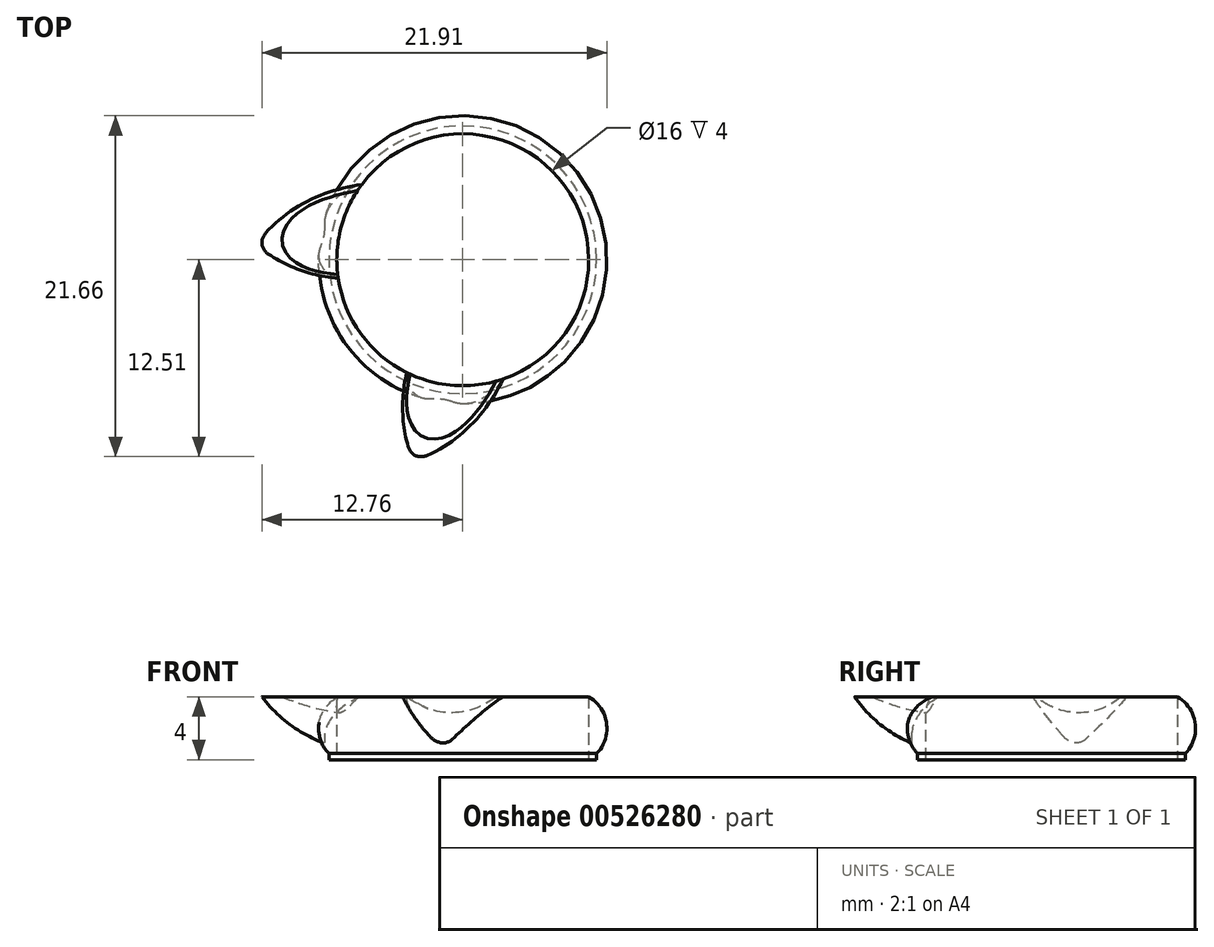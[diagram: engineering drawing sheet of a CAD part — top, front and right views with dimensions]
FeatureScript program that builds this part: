
annotation { "Feature Type Name" : "Feature", "Feature Type Description" : "" }
export const myFeature = defineFeature(function(context is Context, id is Id, definition is map)
    precondition{}
    {
        {
            var Q0;
            Q0=qCreatedBy(makeId("Front.planeOp"),FACE);
            var sketch = newSketch(context, id + "F0", { "sketchPlane" : qUnion([Q0])});
            skArc(sketch, "E0", {"start": v(-8, 2) * mm, "mid": v(-9.15, 0) * mm, "end": v(-8, -2) * mm});
            skLineSegment(sketch, "E1", {"start": v(-8, 2) * mm, "end": v(-8, -2) * mm});
            skLineSegment(sketch, "E2", {"start": v(0, 0) * mm, "end": v(0, 2) * mm, "construction": true});
            skPoint(sketch, "E3", {"position": v(-8, 0) * mm});
            skLineSegment(sketch, "E4", {"start": v(-9.15, 0) * mm, "end": v(-6.85, 0) * mm});
            skLineSegment(sketch, "E5.bottom", {"start": v(-8, -2) * mm, "end": v(-8.5, -2) * mm});
            skLineSegment(sketch, "E5.top", {"start": v(-8, -1.6) * mm, "end": v(-8.5, -1.6) * mm});
            skLineSegment(sketch, "E5.left", {"start": v(-8, -2) * mm, "end": v(-8, -1.6) * mm});
            skLineSegment(sketch, "E5.right", {"start": v(-8.5, -2) * mm, "end": v(-8.5, -1.6) * mm});
            skSolve(sketch);
        }
        {
            var Q0;
            {var subQ0=sQuery(id+"F0.wireOp",EDGE,"E1");var subQ1=sQuery(id+"F0.wireOp",EDGE,"E0");var subQ2=makeQuery(id+"F0.imprint","INTERSECT",VERTEX,{"derivedFrom":[subQ1,subQ0]});Q0=makeQuery(id+"F0.imprint","IMPRINT",FACE,{"disambiguationData":[TD([[makeQuery(id+"F0.imprint","IMPRINT",EDGE,{"disambiguationData":[TD([[subQ2,-1.0]])],"derivedFrom":subQ1}),1.0]])]});}
            var Q1;
            {var subQ3=sQuery(id+"F0.wireOp",EDGE,"E5.top");Q1=makeQuery(id+"F0.imprint","IMPRINT",FACE,{"disambiguationData":[TD([[makeQuery(id+"F0.imprint","IMPRINT",EDGE,{"derivedFrom":subQ3}),-1.0]])]});}
            var Q2;
            {var subQ2=sQuery(id+"F0.wireOp",EDGE,"E5.top");Q2=makeQuery(id+"F0.imprint","IMPRINT",FACE,{"disambiguationData":[TD([[makeQuery(id+"F0.imprint","IMPRINT",EDGE,{"derivedFrom":subQ2}),1.0]])]});}
            var Q3;
            {var subQ0=sQuery(id+"F0.wireOp",EDGE,"E5.bottom");Q3=makeQuery(id+"F0.imprint","IMPRINT",FACE,{"disambiguationData":[TD([[makeQuery(id+"F0.imprint","IMPRINT",EDGE,{"derivedFrom":subQ0}),-1.0]])]});}
            var Q4;
            Q4=sQuery(id+"F0.wireOp",EDGE,"E2");
            revolve(context, id + "F1", {"entities" : qUnion([Q0, Q1, Q2, Q3]), "axis" : qUnion([Q4]), "revolveType" : RevolveType.FULL});
        }
        {
            var Q0;
            Q0=qCreatedBy(makeId("Front.planeOp"),FACE);
            cPlane(context, id + "F2", {"entities" : qUnion([Q0]), "cplaneType" : CPlaneType.OFFSET, "offset" : 6 * mm, "width" : 150 * mm, "height" : 150 * mm});
        }
        {
            var Q0;
            Q0=qCreatedBy(id+"F2.planeOp",FACE);
            var sketch = newSketch(context, id + "F3", { "sketchPlane" : qUnion([Q0])});
            skLineSegment(sketch, "E6", {"start": v(0, 19.97) * mm, "end": v(0, -12.14) * mm});
            skSolve(sketch);
        }
        {
            var Q0;
            Q0=sQuery(id+"F3.wireOp",EDGE,"E6");
            var Q1;
            Q1=qCreatedBy(id+"F2.planeOp",FACE);
            cPlane(context, id + "F4", {"entities" : qUnion([Q0, Q1]), "cplaneType" : CPlaneType.LINE_ANGLE, "offset" : 25 * mm, "angle" : 25 * degree, "width" : 150 * mm, "height" : 150 * mm});
        }
        {
            var Q0;
            Q0=qCreatedBy(id+"F4.planeOp",FACE);
            var sketch = newSketch(context, id + "F5", { "sketchPlane" : qUnion([Q0])});
            skLineSegment(sketch, "E7", {"start": v(-10.54, 7.45) * mm, "end": v(5.46, 7.45) * mm});
            skPoint(sketch, "E8", {"position": v(-2.54, 7.45) * mm});
            skLineSegment(sketch, "E9", {"start": v(-5.54, 2) * mm, "end": v(0.46, 2) * mm});
            skPoint(sketch, "E10", {"position": v(-2.54, 2) * mm});
            skArc(sketch, "E11", {"start": v(-3.2, -1.25) * mm, "mid": v(-2.54, -1.5) * mm, "end": v(-1.88, -1.25) * mm});
            skArc(sketch, "E12", {"start": v(-5.54, 2) * mm, "mid": v(-4.55, 0.24) * mm, "end": v(-3.2, -1.25) * mm});
            skArc(sketch, "E13", {"start": v(-1.88, -1.25) * mm, "mid": v(-0.52, 0.24) * mm, "end": v(0.46, 2) * mm});
            skPoint(sketch, "E14", {"position": v(-2.54, -1.5) * mm});
            skSolve(sketch);
        }
        {
            var Q0;
            Q0=makeQuery(id+"F5.imprint","IMPRINT",FACE,{"disambiguationData":[TD([[makeQuery(id+"F5.imprint","IMPRINT",EDGE,{"derivedFrom":sQuery(id+"F5.wireOp",EDGE,"E9")}),-1.0]])]});
            var Q1;
            Q1=sQuery(id+"F5.wireOp",EDGE,"E7");
            revolve(context, id + "F6", {"operationType" : NewBodyOperationType.ADD, "entities" : qUnion([Q0]), "axis" : qUnion([Q1]), "revolveType" : RevolveType.FULL});
        }
        {
            var Q0;
            Q0=qCreatedBy(makeId("Top.planeOp"),FACE);
            var sketch = newSketch(context, id + "F7", { "sketchPlane" : qUnion([Q0])});
            skCircle(sketch, "E15.0", {"center": v(0, 0) * mm, "radius": 8 * mm});
            skSolve(sketch);
        }
        {
            var Q0;
            Q0=makeQuery(id+"F7.imprint","IMPRINT",FACE,{"disambiguationData":[TD([[makeQuery(id+"F7.imprint","IMPRINT",EDGE,{"derivedFrom":sQuery(id+"F7.wireOp",EDGE,"E15.0")}),1.0]])]});
            extrude(context, id + "F8", {"entities" : qUnion([Q0]), "operationType" : NewBodyOperationType.REMOVE, "endBound" : BoundingType.THROUGH_ALL, "depth" : 25 * mm, "offsetDistance" : 25 * mm, "hasSecondDirection" : true, "secondDirectionBound" : SecondDirectionBoundingType.THROUGH_ALL, "secondDirectionOppositeDirection" : true, "secondDirectionDepth" : 25 * mm});
        }
        {
            var Q0;
            Q0=qCreatedBy(makeId("Top.planeOp"),FACE);
            cPlane(context, id + "F9", {"entities" : qUnion([Q0]), "cplaneType" : CPlaneType.OFFSET, "offset" : 2 * mm, "width" : 150 * mm, "height" : 150 * mm});
        }
        {
            var Q0;
            Q0=qCreatedBy(id+"F9.planeOp",FACE);
            var sketch = newSketch(context, id + "F10", { "sketchPlane" : qUnion([Q0])});
            skLineSegment(sketch, "E16.bottom", {"start": v(-9.55, 0) * mm, "end": v(4.28, 0) * mm});
            skLineSegment(sketch, "E16.top", {"start": v(-9.55, -18.3) * mm, "end": v(4.28, -18.3) * mm});
            skLineSegment(sketch, "E16.left", {"start": v(-9.55, 0) * mm, "end": v(-9.55, -18.3) * mm});
            skLineSegment(sketch, "E16.right", {"start": v(4.28, 0) * mm, "end": v(4.28, -18.3) * mm});
            skSolve(sketch);
        }
        {
            var Q0;
            Q0=makeQuery(id+"F10.imprint","IMPRINT",FACE,{"disambiguationData":[TD([[makeQuery(id+"F10.imprint","IMPRINT",EDGE,{"derivedFrom":sQuery(id+"F10.wireOp",EDGE,"E16.bottom")}),-1.0]])]});
            extrude(context, id + "F11", {"entities" : qUnion([Q0]), "operationType" : NewBodyOperationType.REMOVE, "endBound" : BoundingType.THROUGH_ALL, "depth" : 25 * mm, "offsetDistance" : 25 * mm});
        }
        {
            var Q0;
            Q0=qCreatedBy(makeId("Front.planeOp"),FACE);
            var sketch = newSketch(context, id + "F12", { "sketchPlane" : qUnion([Q0])});
            skLineSegment(sketch, "E17.0", {"start": v(0, 19.97) * mm, "end": v(0, -12.14) * mm});
            skSolve(sketch);
        }
        {
            var Q0;
            Q0=sQuery(id+"F12.wireOp",EDGE,"E17.0");
            var Q1;
            Q1=qCreatedBy(makeId("Front.planeOp"),FACE);
            cPlane(context, id + "F13", {"entities" : qUnion([Q0, Q1]), "cplaneType" : CPlaneType.LINE_ANGLE, "offset" : 25 * mm, "angle" : 36 * degree, "oppositeDirection" : true, "width" : 150 * mm, "height" : 150 * mm});
        }
        {
            var Q0;
            Q0=qCreatedBy(id+"F4.planeOp",FACE);
            var sketch = newSketch(context, id + "F14", { "sketchPlane" : qUnion([Q0])});
            skArc(sketch, "E18", {"start": v(-5.2, 2) * mm, "mid": v(-2.5, 0.84) * mm, "end": v(0.2, 2) * mm});
            skLineSegment(sketch, "E19", {"start": v(0.39, 16) * mm, "end": v(-6.03, 16) * mm});
            skLineSegment(sketch, "E20", {"start": v(-5.2, 2) * mm, "end": v(0.2, 2) * mm});
            skSolve(sketch);
        }
        {
            var Q0;
            Q0=makeQuery(id+"F14.imprint","IMPRINT",FACE,{"disambiguationData":[TD([[makeQuery(id+"F14.imprint","IMPRINT",EDGE,{"derivedFrom":sQuery(id+"F14.wireOp",EDGE,"E18")}),1.0]])]});
            var Q1;
            Q1=sQuery(id+"F14.wireOp",EDGE,"E19");
            revolve(context, id + "F15", {"operationType" : NewBodyOperationType.REMOVE, "entities" : qUnion([Q0]), "axis" : qUnion([Q1]), "revolveType" : RevolveType.FULL, "oppositeDirection" : true});
        }
        {
            var Q0;
            Q0=qCreatedBy(id+"F13.planeOp",FACE);
            var sketch = newSketch(context, id + "F16", { "sketchPlane" : qUnion([Q0])});
            skLineSegment(sketch, "E21.bottom", {"start": v(-12.73, 14.2) * mm, "end": v(12.19, 14.2) * mm});
            skLineSegment(sketch, "E21.top", {"start": v(-12.73, -10.37) * mm, "end": v(12.19, -10.37) * mm});
            skLineSegment(sketch, "E21.left", {"start": v(-12.73, 14.2) * mm, "end": v(-12.73, -10.37) * mm});
            skLineSegment(sketch, "E21.right", {"start": v(12.19, 14.2) * mm, "end": v(12.19, -10.37) * mm});
            skSolve(sketch);
        }
        {
            var Q0;
            Q0=makeQuery(id+"F16.imprint","IMPRINT",FACE,{"disambiguationData":[TD([[makeQuery(id+"F16.imprint","IMPRINT",EDGE,{"derivedFrom":sQuery(id+"F16.wireOp",EDGE,"E21.bottom")}),-1.0]])]});
            extrude(context, id + "F17", {"entities" : qUnion([Q0]), "operationType" : NewBodyOperationType.REMOVE, "depth" : 25 * mm, "offsetDistance" : 25 * mm});
        }
        {
            var Q0;
            Q0=makeQuery(id+"F1.opRevolve","SWEPT_BODY",BODY,{"disambiguationData":[OSD([sQuery(id+"F0.wireOp",EDGE,"E0"),sQuery(id+"F0.wireOp",EDGE,"E1")])]});
            var Q1;
            Q1=qCreatedBy(id+"F13.planeOp",FACE);
            mirror(context, id + "F18", {"operationType" : NewBodyOperationType.ADD, "entities" : qUnion([Q0]), "mirrorPlane" : qUnion([Q1])});
        }
    });
